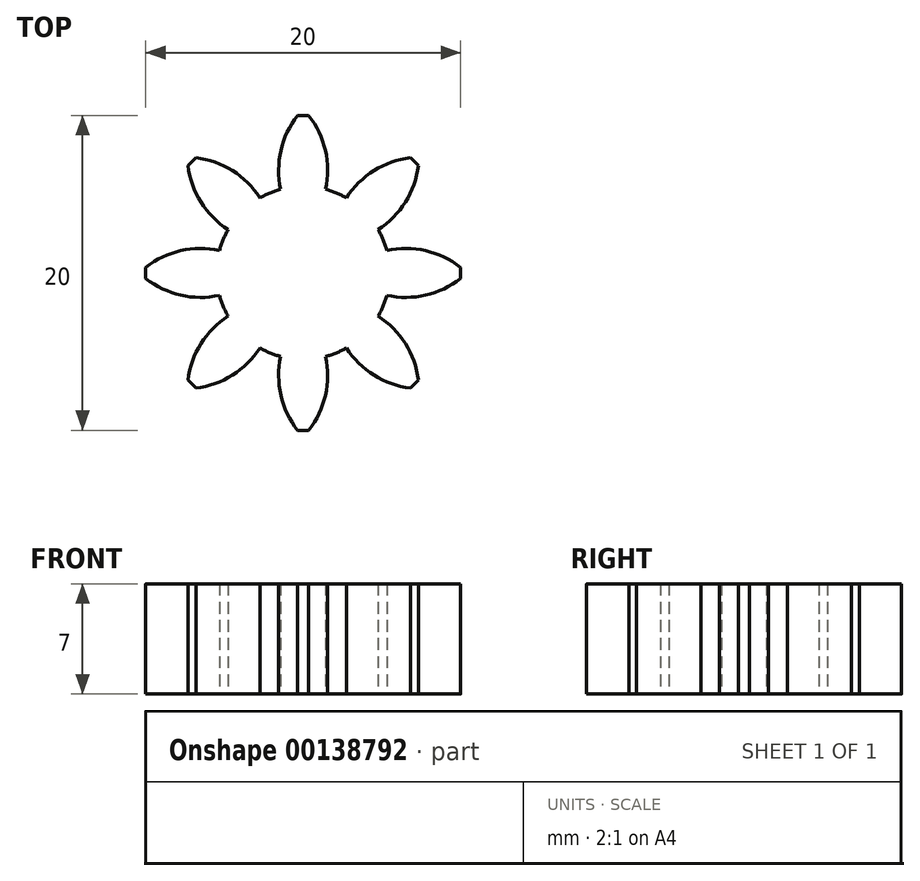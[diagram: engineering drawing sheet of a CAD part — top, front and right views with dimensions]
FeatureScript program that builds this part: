
annotation { "Feature Type Name" : "Feature", "Feature Type Description" : "" }
export const myFeature = defineFeature(function(context is Context, id is Id, definition is map)
    precondition{}
    {
        {
            var Q0;
            Q0=qCreatedBy(makeId("Top.planeOp"),FACE);
            var sketch = newSketch(context, id + "F0", { "sketchPlane" : qUnion([Q0])});
            skCircle(sketch, "E0", {"center": v(0, 0) * mm, "radius": 5.5 * mm});
            skCircle(sketch, "E1", {"center": v(0, 0) * mm, "radius": 8 * mm, "construction": true});
            skLineSegment(sketch, "E2", {"start": v(0, 0) * mm, "end": v(0, 10) * mm, "construction": true});
            skLineSegment(sketch, "E3", {"start": v(0, 0) * mm, "end": v(1.74, 9.85) * mm, "construction": true});
            skLineSegment(sketch, "E4", {"start": v(0, 8) * mm, "end": v(-32.72, 8) * mm, "construction": true});
            skLineSegment(sketch, "E5", {"start": v(0, 8) * mm, "end": v(-31.45, -3.45) * mm, "construction": true});
            skCircle(sketch, "E6", {"center": v(1.39, 7.88) * mm, "radius": 5.62 * mm, "construction": true});
            skArc(sketch, "E7", {"start": v(-2.52, 11.93) * mm, "mid": v(-8.9, 3.64) * mm, "end": v(1.42, 5.31) * mm, "construction": true});
            skArc(sketch, "E8", {"start": v(1.42, 5.31) * mm, "mid": v(1.56, 6.6) * mm, "end": v(1.39, 7.88) * mm});
            skArc(sketch, "E9", {"start": v(0.35, 10) * mm, "mid": v(-0.93, 11.19) * mm, "end": v(-2.52, 11.93) * mm, "construction": true});
            skArc(sketch, "E10", {"start": v(1.39, 7.88) * mm, "mid": v(0.98, 9) * mm, "end": v(0.35, 10) * mm});
            skArc(sketch, "E11", {"start": v(0, 10) * mm, "mid": v(-0.18, 10) * mm, "end": v(-0.35, 10) * mm});
            skArc(sketch, "E12", {"start": v(0.35, 10) * mm, "mid": v(0.18, 10) * mm, "end": v(0, 10) * mm});
            skArc(sketch, "E13.MirrorCS", {"start": v(-0.35, 10) * mm, "mid": v(-0.18, 10) * mm, "end": v(0, 10) * mm, "construction": true});
            skArc(sketch, "E14.MirrorCS", {"start": v(-1.39, 7.88) * mm, "mid": v(-0.99, 8.98) * mm, "end": v(-0.36, 9.98) * mm});
            skArc(sketch, "E15.MirrorCS", {"start": v(-1.42, 5.31) * mm, "mid": v(-1.56, 6.6) * mm, "end": v(-1.39, 7.88) * mm});
            skArc(sketch, "E16", {"start": v(-0.36, 9.98) * mm, "mid": v(-0.36, 9.99) * mm, "end": v(-0.35, 10) * mm});
            skArc(sketch, "E17", {"start": v(0, 10) * mm, "mid": v(0, 10) * mm, "end": v(0, 10) * mm, "construction": true});
            skArc(sketch, "E18", {"start": v(-0.36, 10) * mm, "mid": v(0, -10) * mm, "end": v(0.35, 10) * mm, "construction": true});
            skLineSegment(sketch, "E19", {"start": v(0, 10) * mm, "end": v(0, 10) * mm});
            skArc(sketch, "E20", {"start": v(-0.35, 10) * mm, "mid": v(-0.36, 10) * mm, "end": v(-0.36, 10) * mm, "construction": true});
            skSolve(sketch);
        }
        {
            var Q0;
            Q0=qSketchRegion(id+"F0",true);
            extrude(context, id + "F1", {"entities" : qUnion([Q0]), "depth" : 7 * mm});
        }
        {
            var Q0;
            Q0=qCreatedBy(makeId("Right.planeOp"),FACE);
            var sketch = newSketch(context, id + "F2", { "sketchPlane" : qUnion([Q0])});
            skLineSegment(sketch, "E21", {"start": v(0, 43.93) * mm, "end": v(0, 0) * mm, "construction": true});
            skSolve(sketch);
        }
        {
            var Q0;
            Q0=makeQuery(id+"F1.opExtrude","SWEPT_BODY",BODY,{"disambiguationData":[OSD([sQuery(id+"F0.wireOp",EDGE,"E0"),sQuery(id+"F0.wireOp",EDGE,"E8"),sQuery(id+"F0.wireOp",EDGE,"E10"),sQuery(id+"F0.wireOp",EDGE,"E12"),sQuery(id+"F0.wireOp",EDGE,"E13.MirrorCS"),sQuery(id+"F0.wireOp",EDGE,"E14.MirrorCS"),sQuery(id+"F0.wireOp",EDGE,"E15.MirrorCS")])]});
            var Q1;
            Q1=sQuery(id+"F2.wireOp",EDGE,"E21");
            circularPattern(context, id + "F3", {"entities" : qUnion([Q0]), "axis" : qUnion([Q1]), "angle" : 45 * degree, "instanceCount" : 8});
        }
        {
            var Q0;
            Q0=makeQuery(id+"F3.opPattern","COPY",BODY,{"derivedFrom":makeQuery(id+"F1.opExtrude","SWEPT_BODY",BODY,{"disambiguationData":[OSD([sQuery(id+"F0.wireOp",EDGE,"E0"),sQuery(id+"F0.wireOp",EDGE,"E8"),sQuery(id+"F0.wireOp",EDGE,"E10"),sQuery(id+"F0.wireOp",EDGE,"E11"),sQuery(id+"F0.wireOp",EDGE,"E12"),sQuery(id+"F0.wireOp",EDGE,"E14.MirrorCS"),sQuery(id+"F0.wireOp",EDGE,"E15.MirrorCS"),sQuery(id+"F0.wireOp",EDGE,"E16")])]}),"instanceName":"6"});
            var Q1;
            Q1=makeQuery(id+"F3.opPattern","COPY",BODY,{"derivedFrom":makeQuery(id+"F1.opExtrude","SWEPT_BODY",BODY,{"disambiguationData":[OSD([sQuery(id+"F0.wireOp",EDGE,"E0"),sQuery(id+"F0.wireOp",EDGE,"E8"),sQuery(id+"F0.wireOp",EDGE,"E10"),sQuery(id+"F0.wireOp",EDGE,"E11"),sQuery(id+"F0.wireOp",EDGE,"E12"),sQuery(id+"F0.wireOp",EDGE,"E14.MirrorCS"),sQuery(id+"F0.wireOp",EDGE,"E15.MirrorCS"),sQuery(id+"F0.wireOp",EDGE,"E16")])]}),"instanceName":"5"});
            var Q2;
            Q2=makeQuery(id+"F3.opPattern","COPY",BODY,{"derivedFrom":makeQuery(id+"F1.opExtrude","SWEPT_BODY",BODY,{"disambiguationData":[OSD([sQuery(id+"F0.wireOp",EDGE,"E0"),sQuery(id+"F0.wireOp",EDGE,"E8"),sQuery(id+"F0.wireOp",EDGE,"E10"),sQuery(id+"F0.wireOp",EDGE,"E11"),sQuery(id+"F0.wireOp",EDGE,"E12"),sQuery(id+"F0.wireOp",EDGE,"E14.MirrorCS"),sQuery(id+"F0.wireOp",EDGE,"E15.MirrorCS"),sQuery(id+"F0.wireOp",EDGE,"E16")])]}),"instanceName":"4"});
            var Q3;
            Q3=makeQuery(id+"F3.opPattern","COPY",BODY,{"derivedFrom":makeQuery(id+"F1.opExtrude","SWEPT_BODY",BODY,{"disambiguationData":[OSD([sQuery(id+"F0.wireOp",EDGE,"E0"),sQuery(id+"F0.wireOp",EDGE,"E8"),sQuery(id+"F0.wireOp",EDGE,"E10"),sQuery(id+"F0.wireOp",EDGE,"E11"),sQuery(id+"F0.wireOp",EDGE,"E12"),sQuery(id+"F0.wireOp",EDGE,"E14.MirrorCS"),sQuery(id+"F0.wireOp",EDGE,"E15.MirrorCS"),sQuery(id+"F0.wireOp",EDGE,"E16")])]}),"instanceName":"3"});
            var Q4;
            Q4=makeQuery(id+"F3.opPattern","COPY",BODY,{"derivedFrom":makeQuery(id+"F1.opExtrude","SWEPT_BODY",BODY,{"disambiguationData":[OSD([sQuery(id+"F0.wireOp",EDGE,"E0"),sQuery(id+"F0.wireOp",EDGE,"E8"),sQuery(id+"F0.wireOp",EDGE,"E10"),sQuery(id+"F0.wireOp",EDGE,"E11"),sQuery(id+"F0.wireOp",EDGE,"E12"),sQuery(id+"F0.wireOp",EDGE,"E14.MirrorCS"),sQuery(id+"F0.wireOp",EDGE,"E15.MirrorCS"),sQuery(id+"F0.wireOp",EDGE,"E16")])]}),"instanceName":"2"});
            var Q5;
            Q5=makeQuery(id+"F3.opPattern","COPY",BODY,{"derivedFrom":makeQuery(id+"F1.opExtrude","SWEPT_BODY",BODY,{"disambiguationData":[OSD([sQuery(id+"F0.wireOp",EDGE,"E0"),sQuery(id+"F0.wireOp",EDGE,"E8"),sQuery(id+"F0.wireOp",EDGE,"E10"),sQuery(id+"F0.wireOp",EDGE,"E11"),sQuery(id+"F0.wireOp",EDGE,"E12"),sQuery(id+"F0.wireOp",EDGE,"E14.MirrorCS"),sQuery(id+"F0.wireOp",EDGE,"E15.MirrorCS"),sQuery(id+"F0.wireOp",EDGE,"E16")])]}),"instanceName":"1"});
            var Q6;
            Q6=makeQuery(id+"F1.opExtrude","SWEPT_BODY",BODY,{"disambiguationData":[OSD([sQuery(id+"F0.wireOp",EDGE,"E0"),sQuery(id+"F0.wireOp",EDGE,"E8"),sQuery(id+"F0.wireOp",EDGE,"E10"),sQuery(id+"F0.wireOp",EDGE,"E11"),sQuery(id+"F0.wireOp",EDGE,"E12"),sQuery(id+"F0.wireOp",EDGE,"E14.MirrorCS"),sQuery(id+"F0.wireOp",EDGE,"E15.MirrorCS"),sQuery(id+"F0.wireOp",EDGE,"E16")])]});
            var Q7;
            Q7=makeQuery(id+"F3.opPattern","COPY",BODY,{"derivedFrom":makeQuery(id+"F1.opExtrude","SWEPT_BODY",BODY,{"disambiguationData":[OSD([sQuery(id+"F0.wireOp",EDGE,"E0"),sQuery(id+"F0.wireOp",EDGE,"E8"),sQuery(id+"F0.wireOp",EDGE,"E10"),sQuery(id+"F0.wireOp",EDGE,"E11"),sQuery(id+"F0.wireOp",EDGE,"E12"),sQuery(id+"F0.wireOp",EDGE,"E14.MirrorCS"),sQuery(id+"F0.wireOp",EDGE,"E15.MirrorCS"),sQuery(id+"F0.wireOp",EDGE,"E16")])]}),"instanceName":"7"});
            booleanBodies(context, id + "F4", {"operationType" : BooleanOperationType.UNION, "tools" : qUnion([Q0, Q1, Q2, Q3, Q4, Q5, Q6, Q7])});
        }
    });
